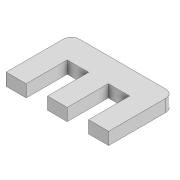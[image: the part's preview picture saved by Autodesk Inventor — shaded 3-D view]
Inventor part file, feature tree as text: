
AUTODESK INVENTOR PART (.ipt)
format: ipt  version: 2022 (Build 260153000, 153)  size: 126,464 bytes
history: native  units: mm
features: extrude x1, fillet x1, thicken_offset x1, sketch x1
ambient origin geometry x8: Origin, YZ Plane, XZ Plane, XY Plane, X Axis, Y Axis, Z Axis, Center Point
bodies: Solid1 (feature_tree)
feature tree (4):
  extrude  "Extrusion1"  Depth=3.0mm
  fillet  "Fillet1"  Radius=25.0mm
  thicken_offset  "Thicken3"
  sketch  "Sketch1"  dims[d0=3.0mm d1=3.0mm d3=25.0mm d4=2.0mm d5=8.0mm d6=6.0mm d7=5.0mm d9=3.0mm d10=9.9mm d11=5.0mm d12=10.0mm d13=5.0mm d14=5.0mm d15=5.0mm d16=6.0mm d17=3.0mm d18=0.0mm d19=5.0mm d20=2.0mm d35=0.1mm d36=0.1mm]
